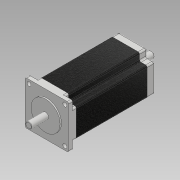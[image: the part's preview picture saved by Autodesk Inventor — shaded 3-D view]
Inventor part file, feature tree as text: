
AUTODESK INVENTOR PART (.ipt)
format: ipt  version: 2018 (Build 220112000, 112)  size: 306,176 bytes
history: native  units: mm
features: extrude x7, sketch x7, fillet x2, chamfer x2, plane x2, split x2, hole x1
ambient origin geometry x8: Origin, YZ Plane, XZ Plane, XY Plane, X Axis, Y Axis, Z Axis, Center Point
bodies: Solid1 (feature_tree)
feature tree (23):
  extrude  "Extrusion1"  Depth=57.0mm
  extrude  "Extrusion2"  Depth=47.0mm
  fillet  "Fillet1"  Radius=47.0mm
  fillet  "Fillet2"  Radius=108.0mm
  hole  "Hole1"  [1 undecoded]
  extrude  "Extrusion3"  Depth=47.0mm
  extrude  "Extrusion4"  Depth=10.0mm
  extrude  "Extrusion5"  Depth=8.0mm
  chamfer  "Chamfer1"  Distance=24.0mm
  plane  "Work Plane1"
  plane  "Work Plane2"
  split  "Split1"
  split  "Split2"
  sketch  "Sketch7"  dims[d25=3.5mm d26=20.0mm d27=0.0mm d28=0.5mm d29=2.0mm d30=45.0deg d31=-10.0mm d32=-10.0mm d33=24.0mm d34=0.0mm d35=4.0mm d36=0.0mm d37=0.5mm d38=2.0mm d39=45.0deg]
  extrude  "Extrusion6"  Depth=20.0mm TaperAngle=0.0deg
  extrude  "Extrusion7"  Depth=20.0mm TaperAngle=45.0deg
  chamfer  "Chamfer2"  [1 undecoded]
  sketch  "Sketch1"  dims[d0=57.0mm d1=57.0mm]
  sketch  "Sketch2"  dims[d2=113.0mm d3=0.0mm d4=47.0mm d5=47.0mm d6=108.0mm d7=0.0mm]
  sketch  "Sketch3"  dims[d8=2.0mm d9=2.0mm]
  sketch  "Sketch4"  dims[d10=47.0mm d11=47.0mm]
  sketch  "Sketch5"  dims[d12=5.3mm d13=6.0mm d14=10.0mm d15=5.0mm d16=90.0deg d17=8.0mm d18=20.594885mm d19=38.1mm]
  sketch  "Sketch6"  dims[d20=1.8mm d21=0.0mm d22=8.0mm d23=24.0mm d24=0.0mm]
note: 2 required parameter values undecoded (feature->parameter linkage not recoverable at this tier; creation-order binding heuristic only, values carry confidence <= 0.55)
